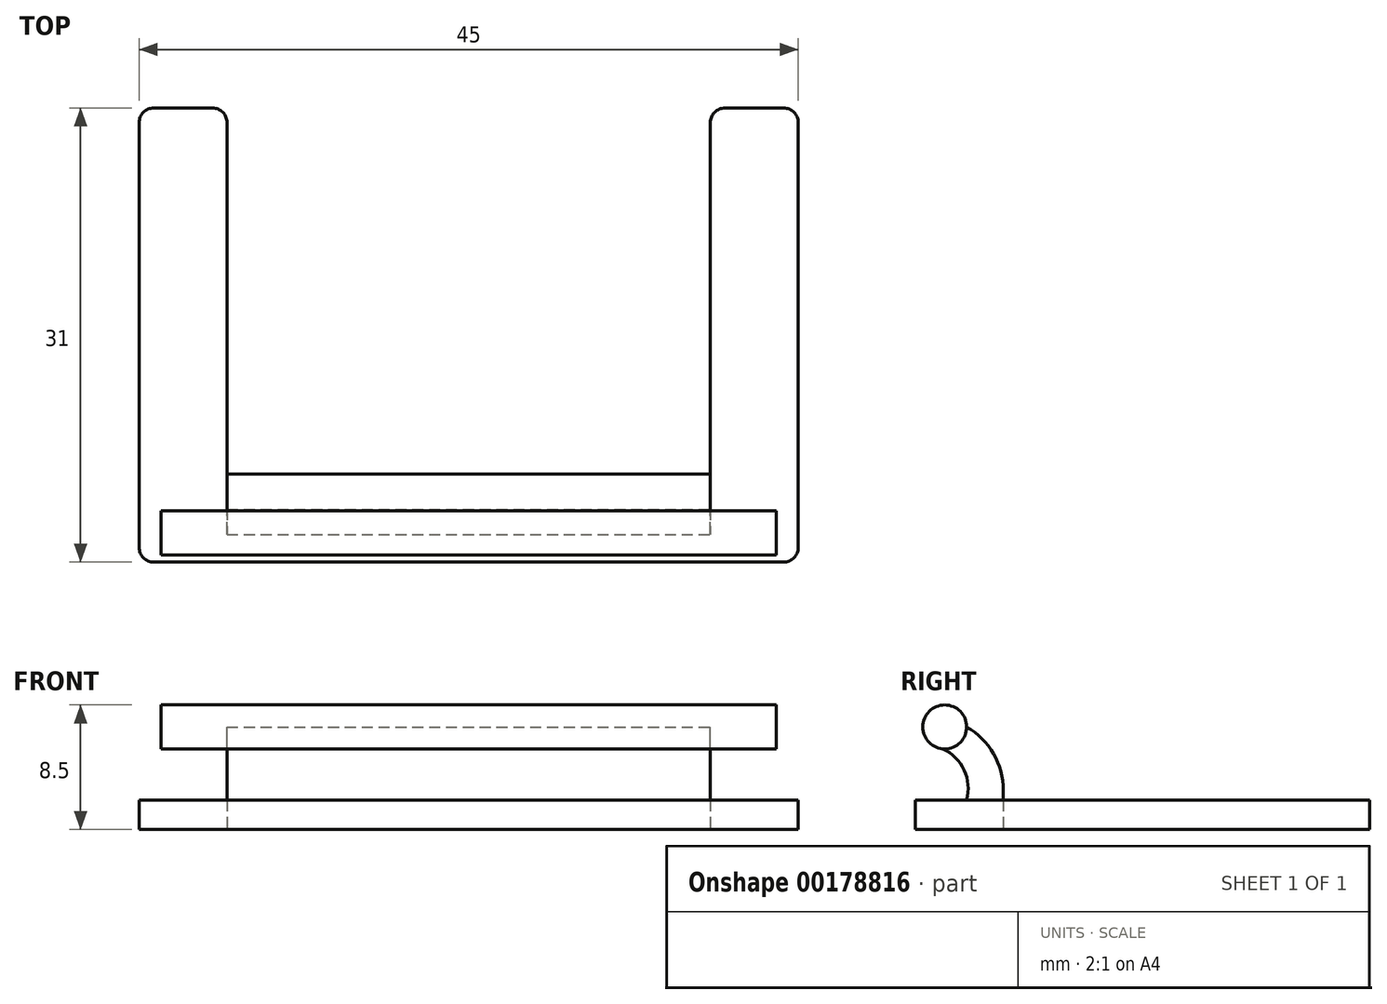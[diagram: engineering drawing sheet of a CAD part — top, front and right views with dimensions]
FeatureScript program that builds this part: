
annotation { "Feature Type Name" : "Feature", "Feature Type Description" : "" }
export const myFeature = defineFeature(function(context is Context, id is Id, definition is map)
    precondition{}
    {
        {
            var Q0;
            Q0=qCreatedBy(makeId("Top.planeOp"),FACE);
            var sketch = newSketch(context, id + "F0", { "sketchPlane" : qUnion([Q0])});
            skLineSegment(sketch, "E0.bottom", {"start": v(21.5, -15.5) * mm, "end": v(-21.5, -15.5) * mm});
            skLineSegment(sketch, "E0.left", {"start": v(22.5, -14.5) * mm, "end": v(22.5, 14.5) * mm});
            skLineSegment(sketch, "E0.right", {"start": v(-22.5, -14.5) * mm, "end": v(-22.5, 14.5) * mm});
            skPoint(sketch, "E0.middle", {"position": v(0, 0) * mm});
            skLineSegment(sketch, "E1.top", {"start": v(-16.5, -9.5) * mm, "end": v(16.5, -9.5) * mm});
            skLineSegment(sketch, "E1.left", {"start": v(-16.5, 14.5) * mm, "end": v(-16.5, -9.5) * mm});
            skLineSegment(sketch, "E1.right", {"start": v(16.5, 14.5) * mm, "end": v(16.5, -9.5) * mm});
            skLineSegment(sketch, "E2", {"start": v(-21.5, 15.5) * mm, "end": v(-17.5, 15.5) * mm});
            skLineSegment(sketch, "E3", {"start": v(17.5, 15.5) * mm, "end": v(21.5, 15.5) * mm});
            skPoint(sketch, "E4.visualSharp", {"position": v(-22.5, 15.5) * mm});
            skArc(sketch, "E4.filletArc", {"start": v(-21.5, 15.5) * mm, "mid": v(-22.2, 15.2) * mm, "end": v(-22.5, 14.5) * mm});
            skPoint(sketch, "E5.visualSharp", {"position": v(-16.5, 15.5) * mm});
            skArc(sketch, "E5.filletArc", {"start": v(-16.5, 14.5) * mm, "mid": v(-16.8, 15.2) * mm, "end": v(-17.5, 15.5) * mm});
            skPoint(sketch, "E6.visualSharp", {"position": v(-22.5, -15.5) * mm});
            skArc(sketch, "E6.filletArc", {"start": v(-22.5, -14.5) * mm, "mid": v(-22.2, -15.2) * mm, "end": v(-21.5, -15.5) * mm});
            skPoint(sketch, "E7.visualSharp", {"position": v(22.5, -15.5) * mm});
            skArc(sketch, "E7.filletArc", {"start": v(21.5, -15.5) * mm, "mid": v(22.2, -15.2) * mm, "end": v(22.5, -14.5) * mm});
            skPoint(sketch, "E8.visualSharp", {"position": v(22.5, 15.5) * mm});
            skArc(sketch, "E8.filletArc", {"start": v(22.5, 14.5) * mm, "mid": v(22.2, 15.2) * mm, "end": v(21.5, 15.5) * mm});
            skPoint(sketch, "E9.visualSharp", {"position": v(16.5, 15.5) * mm});
            skArc(sketch, "E9.filletArc", {"start": v(17.5, 15.5) * mm, "mid": v(16.8, 15.2) * mm, "end": v(16.5, 14.5) * mm});
            skSolve(sketch);
        }
        {
            var Q0;
            Q0=qSketchRegion(id+"F0",true);
            extrude(context, id + "F1", {"entities" : qUnion([Q0]), "depth" : 2 * mm});
        }
        {
            var Q0;
            Q0=makeQuery(id+"F1.opExtrude","CAP_FACE",FACE,{"disambiguationData":[OSD([sQuery(id+"F0.wireOp",EDGE,"E0.bottom"),sQuery(id+"F0.wireOp",EDGE,"E0.left"),sQuery(id+"F0.wireOp",EDGE,"E0.right"),sQuery(id+"F0.wireOp",EDGE,"E1.top"),sQuery(id+"F0.wireOp",EDGE,"E1.left"),sQuery(id+"F0.wireOp",EDGE,"E1.right"),sQuery(id+"F0.wireOp",EDGE,"E2"),sQuery(id+"F0.wireOp",EDGE,"E3")])],"isStart":false});
            var sketch = newSketch(context, id + "F2", { "sketchPlane" : qUnion([Q0])});
            skLineSegment(sketch, "E10.bottom", {"start": v(-16.5, -9.5) * mm, "end": v(16.5, -9.5) * mm});
            skLineSegment(sketch, "E10.top", {"start": v(-16.5, -14.5) * mm, "end": v(16.5, -14.5) * mm});
            skLineSegment(sketch, "E10.left", {"start": v(-16.5, -9.5) * mm, "end": v(-16.5, -14.5) * mm});
            skLineSegment(sketch, "E10.right", {"start": v(16.5, -9.5) * mm, "end": v(16.5, -14.5) * mm});
            skSolve(sketch);
        }
        {
            var Q0;
            Q0=qSketchRegion(id+"F2",true);
            extrude(context, id + "F3", {"entities" : qUnion([Q0]), "operationType" : NewBodyOperationType.ADD, "depth" : 5 * mm});
        }
        {
            var Q0;
            Q0=makeQuery(id+"F3.opExtrude","SWEPT_FACE",FACE,{"disambiguationData":[OSD([sQuery(id+"F2.wireOp",EDGE,"E10.right")])]});
            cPlane(context, id + "F4", {"entities" : qUnion([Q0]), "cplaneType" : CPlaneType.OFFSET, "offset" : 4.5 * mm, "width" : 150 * mm, "height" : 150 * mm});
        }
        {
            var Q0;
            Q0=makeQuery(id+"F3.opExtrude","SWEPT_FACE",FACE,{"disambiguationData":[OSD([sQuery(id+"F2.wireOp",EDGE,"E10.left")])]});
            cPlane(context, id + "F5", {"entities" : qUnion([Q0]), "cplaneType" : CPlaneType.OFFSET, "offset" : 4.5 * mm, "width" : 150 * mm, "height" : 150 * mm});
        }
        {
            var Q0;
            Q0=qCreatedBy(id+"F4.planeOp",FACE);
            var sketch = newSketch(context, id + "F6", { "sketchPlane" : qUnion([Q0])});
            skCircle(sketch, "E11", {"center": v(-13.5, 7) * mm, "radius": 1.5 * mm});
            skSolve(sketch);
        }
        {
            var Q0;
            Q0=qSketchRegion(id+"F6",true);
            var Q1;
            Q1=qCreatedBy(id+"F5.planeOp",FACE);
            extrude(context, id + "F7", {"entities" : qUnion([Q0]), "operationType" : NewBodyOperationType.ADD, "endBound" : BoundingType.UP_TO_SURFACE, "oppositeDirection" : true, "endBoundEntityFace" : qUnion([Q1]), "depth" : 25 * mm});
        }
        {
            var Q0;
            Q0=makeQuery(id+"F3.opExtrude","CAP_EDGE",EDGE,{"disambiguationData":[OSD([sQuery(id+"F2.wireOp",EDGE,"E10.bottom")])],"isStart":false});
            fillet(context, id + "F8", {"entities" : qUnion([Q0]), "radius" : 5 * mm, "tangentPropagation" : true, "allowEdgeOverflow" : false});
        }
        {
            var Q0;
            Q0=makeQuery(id+"F3.opExtrude","SWEPT_FACE",FACE,{"disambiguationData":[OSD([sQuery(id+"F2.wireOp",EDGE,"E10.right")])]});
            var sketch = newSketch(context, id + "F9", { "sketchPlane" : qUnion([Q0])});
            skLineSegment(sketch, "E12.0", {"start": v(-14.5, 5.88) * mm, "end": v(-14.5, 2) * mm});
            skLineSegment(sketch, "E13.0", {"start": v(-9.5, 2) * mm, "end": v(-14.5, 2) * mm});
            skArc(sketch, "E14", {"start": v(-12, 2) * mm, "mid": v(-12.17, 4.05) * mm, "end": v(-13.63, 5.5) * mm});
            skArc(sketch, "E15.0", {"start": v(-14.5, 5.88) * mm, "mid": v(-14.1, 5.62) * mm, "end": v(-13.63, 5.5) * mm});
            skPoint(sketch, "E16.orphan", {"position": v(-12, 7) * mm});
            skSolve(sketch);
        }
        {
            var Q0;
            Q0 = qSketchRegion(id + "F9", true);
            extrude(context, id + "F10", {"entities" : qUnion([Q0]), "operationType" : NewBodyOperationType.REMOVE, "endBound" : BoundingType.THROUGH_ALL, "oppositeDirection" : true, "depth" : 25 * mm});
        }
    });
